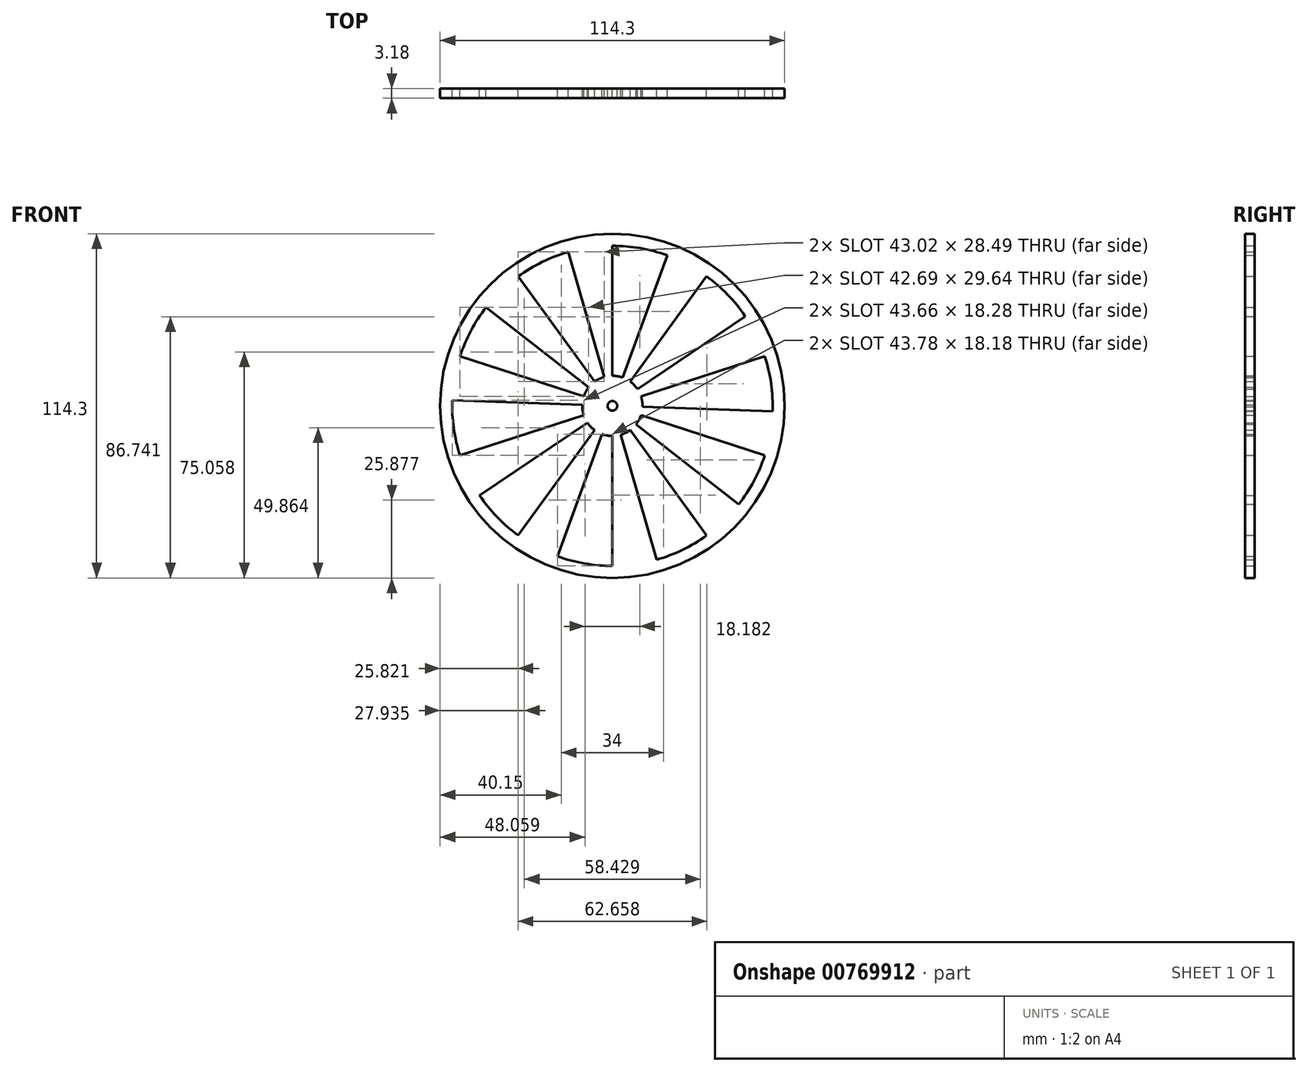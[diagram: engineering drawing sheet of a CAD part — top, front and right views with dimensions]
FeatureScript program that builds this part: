
annotation { "Feature Type Name" : "Feature", "Feature Type Description" : "" }
export const myFeature = defineFeature(function(context is Context, id is Id, definition is map)
    precondition{}
    {
        {
            var Q0;
            Q0=qCreatedBy(makeId("Front.planeOp"),FACE);
            var sketch = newSketch(context, id + "F0", { "sketchPlane" : qUnion([Q0])});
            skCircle(sketch, "E0", {"center": v(0, 0) * mm, "radius": 57.15 * mm});
            skArc(sketch, "E1", {"start": v(18.18, 49.96) * mm, "mid": v(9.23, 52.35) * mm, "end": v(0, 53.16) * mm});
            skArc(sketch, "E2", {"start": v(3.42, 9.39) * mm, "mid": v(1.73, 9.84) * mm, "end": v(0, 9.99) * mm});
            skLineSegment(sketch, "E3", {"start": v(0, 9.99) * mm, "end": v(0, 53.16) * mm});
            skLineSegment(sketch, "E4", {"start": v(3.42, 9.39) * mm, "end": v(18.18, 49.96) * mm});
            skArc(sketch, "E5.1.0", {"start": v(-14.65, 51.1) * mm, "mid": v(-23.3, 47.78) * mm, "end": v(-31.25, 43) * mm});
            skLineSegment(sketch, "E5.1.1", {"start": v(-5.87, 8.08) * mm, "end": v(-31.25, 43) * mm});
            skArc(sketch, "E5.1.2", {"start": v(-2.75, 9.6) * mm, "mid": v(-4.38, 8.98) * mm, "end": v(-5.87, 8.08) * mm});
            skLineSegment(sketch, "E5.1.3", {"start": v(-2.75, 9.6) * mm, "end": v(-14.65, 51.1) * mm});
            skArc(sketch, "E5.2.0", {"start": v(-41.9, 32.73) * mm, "mid": v(-46.94, 24.96) * mm, "end": v(-50.56, 16.43) * mm});
            skLineSegment(sketch, "E5.2.1", {"start": v(-9.5, 3.09) * mm, "end": v(-50.56, 16.43) * mm});
            skArc(sketch, "E5.2.2", {"start": v(-7.87, 6.15) * mm, "mid": v(-8.82, 4.69) * mm, "end": v(-9.5, 3.09) * mm});
            skLineSegment(sketch, "E5.2.3", {"start": v(-7.87, 6.15) * mm, "end": v(-41.9, 32.73) * mm});
            skArc(sketch, "E5.3.0", {"start": v(-53.13, 1.86) * mm, "mid": v(-52.64, -7.4) * mm, "end": v(-50.56, -16.43) * mm});
            skLineSegment(sketch, "E5.3.1", {"start": v(-9.5, -3.09) * mm, "end": v(-50.56, -16.43) * mm});
            skArc(sketch, "E5.3.2", {"start": v(-9.98, 0.35) * mm, "mid": v(-9.9, -1.39) * mm, "end": v(-9.5, -3.09) * mm});
            skLineSegment(sketch, "E5.3.3", {"start": v(-9.98, 0.35) * mm, "end": v(-53.13, 1.86) * mm});
            skArc(sketch, "E5.4.0", {"start": v(-44.07, -29.73) * mm, "mid": v(-38.24, -36.93) * mm, "end": v(-31.25, -43) * mm});
            skLineSegment(sketch, "E5.4.1", {"start": v(-5.87, -8.08) * mm, "end": v(-31.25, -43) * mm});
            skArc(sketch, "E5.4.2", {"start": v(-8.28, -5.58) * mm, "mid": v(-7.18, -6.94) * mm, "end": v(-5.87, -8.08) * mm});
            skLineSegment(sketch, "E5.4.3", {"start": v(-8.28, -5.58) * mm, "end": v(-44.07, -29.73) * mm});
            skArc(sketch, "E5.5.0", {"start": v(-18.18, -49.96) * mm, "mid": v(-9.23, -52.35) * mm, "end": v(0, -53.16) * mm});
            skLineSegment(sketch, "E5.5.1", {"start": v(0, -9.99) * mm, "end": v(0, -53.16) * mm});
            skArc(sketch, "E5.5.2", {"start": v(-3.42, -9.39) * mm, "mid": v(-1.73, -9.84) * mm, "end": v(0, -9.99) * mm});
            skLineSegment(sketch, "E5.5.3", {"start": v(-3.42, -9.39) * mm, "end": v(-18.18, -49.96) * mm});
            skArc(sketch, "E5.6.0", {"start": v(14.65, -51.1) * mm, "mid": v(23.3, -47.78) * mm, "end": v(31.25, -43) * mm});
            skLineSegment(sketch, "E5.6.1", {"start": v(5.87, -8.08) * mm, "end": v(31.25, -43) * mm});
            skArc(sketch, "E5.6.2", {"start": v(2.75, -9.6) * mm, "mid": v(4.38, -8.98) * mm, "end": v(5.87, -8.08) * mm});
            skLineSegment(sketch, "E5.6.3", {"start": v(2.75, -9.6) * mm, "end": v(14.65, -51.1) * mm});
            skArc(sketch, "E5.7.0", {"start": v(41.9, -32.73) * mm, "mid": v(46.94, -24.96) * mm, "end": v(50.56, -16.43) * mm});
            skLineSegment(sketch, "E5.7.1", {"start": v(9.5, -3.09) * mm, "end": v(50.56, -16.43) * mm});
            skArc(sketch, "E5.7.2", {"start": v(7.87, -6.15) * mm, "mid": v(8.82, -4.69) * mm, "end": v(9.5, -3.09) * mm});
            skLineSegment(sketch, "E5.7.3", {"start": v(7.87, -6.15) * mm, "end": v(41.9, -32.73) * mm});
            skArc(sketch, "E5.8.0", {"start": v(53.13, -1.86) * mm, "mid": v(52.64, 7.4) * mm, "end": v(50.56, 16.43) * mm});
            skLineSegment(sketch, "E5.8.1", {"start": v(9.5, 3.09) * mm, "end": v(50.56, 16.43) * mm});
            skArc(sketch, "E5.8.2", {"start": v(9.98, -0.35) * mm, "mid": v(9.9, 1.39) * mm, "end": v(9.5, 3.09) * mm});
            skLineSegment(sketch, "E5.8.3", {"start": v(9.98, -0.35) * mm, "end": v(53.13, -1.86) * mm});
            skArc(sketch, "E5.9.0", {"start": v(44.07, 29.73) * mm, "mid": v(38.24, 36.93) * mm, "end": v(31.25, 43) * mm});
            skLineSegment(sketch, "E5.9.1", {"start": v(5.87, 8.08) * mm, "end": v(31.25, 43) * mm});
            skArc(sketch, "E5.9.2", {"start": v(8.28, 5.58) * mm, "mid": v(7.18, 6.94) * mm, "end": v(5.87, 8.08) * mm});
            skLineSegment(sketch, "E5.9.3", {"start": v(8.28, 5.58) * mm, "end": v(44.07, 29.73) * mm});
            skCircle(sketch, "E6", {"center": v(0, 0) * mm, "radius": 1.59 * mm});
            skSolve(sketch);
        }
        {
            var Q0;
            Q0=makeQuery(id+"F0.imprint","IMPRINT",FACE,{"disambiguationData":[TD([[makeQuery(id+"F0.imprint","IMPRINT",EDGE,{"derivedFrom":sQuery(id+"F0.wireOp",EDGE,"E0")}),1.0]])]});
            extrude(context, id + "F1", {"entities" : qUnion([Q0]), "depth" : 3.17 * mm, "offsetDistance" : 25.4 * mm});
        }
    });
